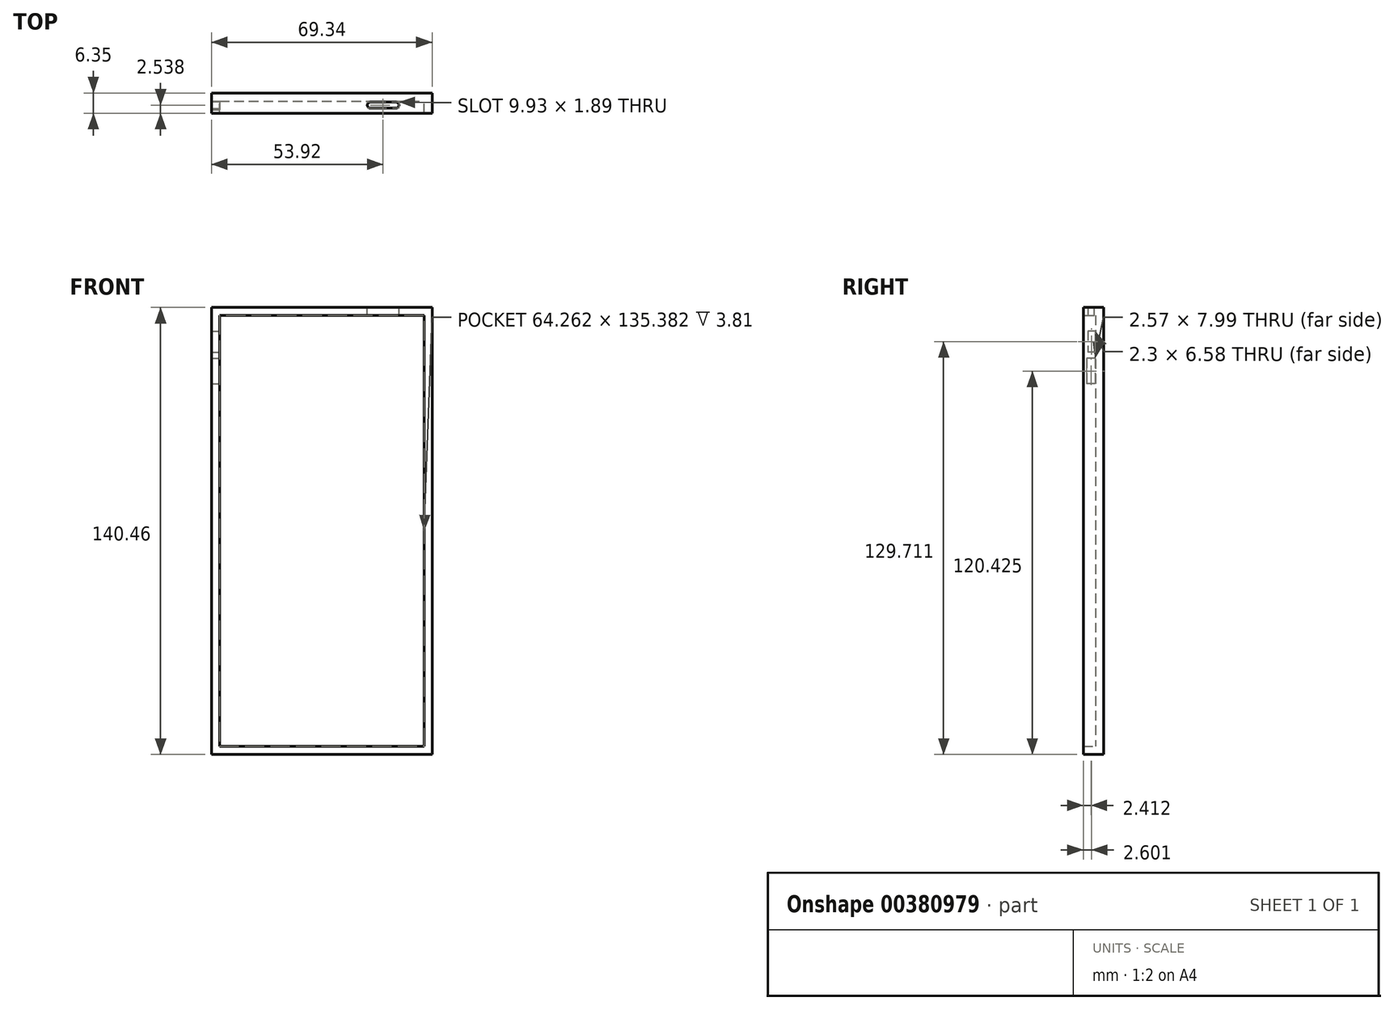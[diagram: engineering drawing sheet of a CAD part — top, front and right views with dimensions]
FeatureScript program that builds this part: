
annotation { "Feature Type Name" : "Feature", "Feature Type Description" : "" }
export const myFeature = defineFeature(function(context is Context, id is Id, definition is map)
    precondition{}
    {
        {
            var Q0;
            Q0=qCreatedBy(makeId("Front.planeOp"),FACE);
            var sketch = newSketch(context, id + "F0", { "sketchPlane" : qUnion([Q0])});
            skLineSegment(sketch, "E0", {"start": v(-34.67, 100.92) * mm, "end": v(-34.67, -39.54) * mm});
            skLineSegment(sketch, "E1", {"start": v(34.67, -39.54) * mm, "end": v(34.67, 100.92) * mm});
            skLineSegment(sketch, "E2", {"start": v(-34.67, 100.92) * mm, "end": v(34.67, 100.92) * mm});
            skLineSegment(sketch, "E3", {"start": v(-34.67, -39.54) * mm, "end": v(34.67, -39.54) * mm});
            skLineSegment(sketch, "E4", {"start": v(0, 100.92) * mm, "end": v(0, -39.54) * mm, "construction": true});
            skSolve(sketch);
        }
        {
            var Q0;
            Q0 = qSketchRegion(id + "F0", true);
            extrude(context, id + "F1", {"entities" : qUnion([Q0]), "depth" : 6.35 * mm});
        }
        {
            var Q0;
            Q0=makeQuery(id+"F1.opExtrude","CAP_FACE",FACE,{"disambiguationData":[OSD([sQuery(id+"F0.wireOp",EDGE,"E0"),sQuery(id+"F0.wireOp",EDGE,"E1"),sQuery(id+"F0.wireOp",EDGE,"E2"),sQuery(id+"F0.wireOp",EDGE,"E3")])],"isStart":false});
            shell(context, id + "F2", {"entities" : qUnion([Q0]), "thickness" : 2.54 * mm});
        }
        {
            var Q0;
            Q0=makeQuery(id+"F1.opExtrude","SWEPT_FACE",FACE,{"disambiguationData":[OSD([sQuery(id+"F0.wireOp",EDGE,"E2")])]});
            var sketch = newSketch(context, id + "F3", { "sketchPlane" : qUnion([Q0])});
            skLineSegment(sketch, "E5.bottom", {"start": v(23.27, -2.87) * mm, "end": v(15.23, -2.87) * mm});
            skLineSegment(sketch, "E5.top", {"start": v(23.27, -4.76) * mm, "end": v(15.23, -4.76) * mm});
            skLineSegment(sketch, "E5.left", {"start": v(23.27, -2.87) * mm, "end": v(23.27, -4.76) * mm});
            skLineSegment(sketch, "E5.right", {"start": v(15.23, -2.87) * mm, "end": v(15.23, -4.76) * mm});
            skCircle(sketch, "E6", {"center": v(23.27, -3.81) * mm, "radius": 0.94 * mm});
            skCircle(sketch, "E7", {"center": v(15.23, -3.81) * mm, "radius": 0.94 * mm});
            skSolve(sketch);
        }
        {
            var Q0;
            Q0 = qSketchRegion(id + "F3", true);
            extrude(context, id + "F4", {"entities" : qUnion([Q0]), "operationType" : NewBodyOperationType.REMOVE, "oppositeDirection" : true, "depth" : 25.4 * mm});
        }
        {
            var Q0;
            Q0=qCreatedBy(makeId("Right.planeOp"),FACE);
            var sketch = newSketch(context, id + "F5", { "sketchPlane" : qUnion([Q0])});
            skLineSegment(sketch, "E8.bottom", {"start": v(-2.6, 93.46) * mm, "end": v(-4.9, 93.46) * mm});
            skLineSegment(sketch, "E8.top", {"start": v(-2.6, 86.88) * mm, "end": v(-4.9, 86.88) * mm});
            skLineSegment(sketch, "E8.left", {"start": v(-2.6, 93.46) * mm, "end": v(-2.6, 86.88) * mm});
            skLineSegment(sketch, "E8.right", {"start": v(-4.9, 93.46) * mm, "end": v(-4.9, 86.88) * mm});
            skLineSegment(sketch, "E9.bottom", {"start": v(-2.65, 84.88) * mm, "end": v(-5.22, 84.88) * mm});
            skLineSegment(sketch, "E9.top", {"start": v(-2.65, 76.89) * mm, "end": v(-5.22, 76.89) * mm});
            skLineSegment(sketch, "E9.left", {"start": v(-2.65, 84.88) * mm, "end": v(-2.65, 76.89) * mm});
            skLineSegment(sketch, "E9.right", {"start": v(-5.22, 84.88) * mm, "end": v(-5.22, 76.89) * mm});
            skSolve(sketch);
        }
        {
            var Q0;
            Q0 = qSketchRegion(id + "F5", true);
            extrude(context, id + "F6", {"entities" : qUnion([Q0]), "operationType" : NewBodyOperationType.REMOVE, "oppositeDirection" : true, "depth" : 38.1 * mm});
        }
    });
